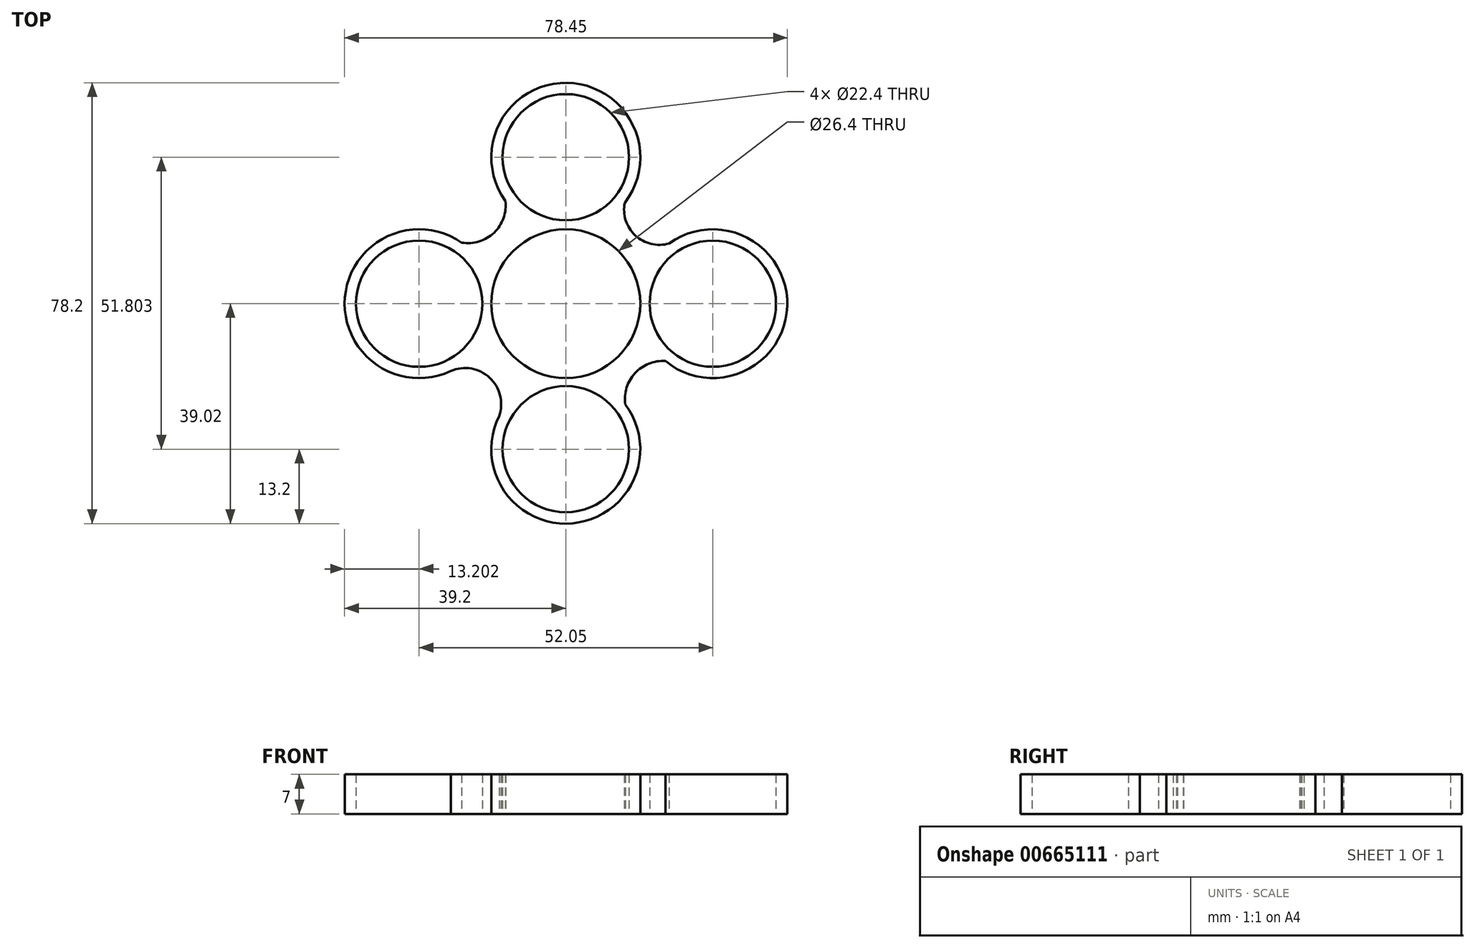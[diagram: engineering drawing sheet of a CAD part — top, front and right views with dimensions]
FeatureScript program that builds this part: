
annotation { "Feature Type Name" : "Feature", "Feature Type Description" : "" }
export const myFeature = defineFeature(function(context is Context, id is Id, definition is map)
    precondition{}
    {
        {
            var Q0;
            Q0=qCreatedBy(makeId("Top.planeOp"),FACE);
            var sketch = newSketch(context, id + "F0", { "sketchPlane" : qUnion([Q0])});
            skCircle(sketch, "E0", {"center": v(0, 0) * mm, "radius": 11.2 * mm});
            skCircle(sketch, "E1", {"center": v(0, 0) * mm, "radius": 13.2 * mm});
            skCircle(sketch, "E2", {"center": v(-26, 0) * mm, "radius": 11.2 * mm});
            skCircle(sketch, "E3", {"center": v(-26, 0) * mm, "radius": 13.2 * mm});
            skCircle(sketch, "E4", {"center": v(26.05, 0) * mm, "radius": 11.2 * mm});
            skCircle(sketch, "E5", {"center": v(26.05, 0) * mm, "radius": 13.2 * mm});
            skCircle(sketch, "E6", {"center": v(0, 25.98) * mm, "radius": 11.2 * mm});
            skCircle(sketch, "E7", {"center": v(0, 25.98) * mm, "radius": 13.2 * mm});
            skCircle(sketch, "E8", {"center": v(0, -25.82) * mm, "radius": 11.2 * mm});
            skCircle(sketch, "E9", {"center": v(0, -25.82) * mm, "radius": 13.2 * mm});
            skArc(sketch, "E10", {"start": v(-21.95, 12.56) * mm, "mid": v(-12.53, 12.78) * mm, "end": v(-12.65, 22.2) * mm});
            skArc(sketch, "E11", {"start": v(-11.8, -19.92) * mm, "mid": v(-13.58, -13.05) * mm, "end": v(-20.6, -12.05) * mm});
            skArc(sketch, "E12", {"start": v(22.5, -12.71) * mm, "mid": v(12.68, -11.92) * mm, "end": v(12.56, -21.77) * mm});
            skArc(sketch, "E13", {"start": v(12.3, 21.2) * mm, "mid": v(12, 12.4) * mm, "end": v(20.8, 12.11) * mm});
            skSolve(sketch);
        }
        {
            var Q0;
            Q0 = qSketchRegion(id + "F0", true);
            extrude(context, id + "F1", {"entities" : qUnion([Q0]), "depth" : 7 * mm, "offsetDistance" : 25 * mm});
        }
    });
